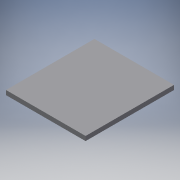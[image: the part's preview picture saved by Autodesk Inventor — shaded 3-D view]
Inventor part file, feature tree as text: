
AUTODESK INVENTOR PART (.ipt)
format: ipt  version: 2018.3 (Build 223284000, 284)  size: 82,944 bytes
history: native  units: mm
features: extrude x1, sketch x1
ambient origin geometry x8: Origin, YZ Plane, XZ Plane, XY Plane, X Axis, Y Axis, Z Axis, Center Point
bodies: Solid1 (feature_tree)
feature tree (2):
  extrude  "Extrusion1"  Depth=40.0mm
  sketch  "Sketch1"  dims[d0=36.0mm d1=40.0mm d2=2.0mm d3=0.0mm]
